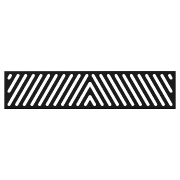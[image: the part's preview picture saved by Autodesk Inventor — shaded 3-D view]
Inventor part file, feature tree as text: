
AUTODESK INVENTOR PART (.ipt)
format: ipt  version: 2015 (Build 190159000, 159)  size: 502,272 bytes
history: native  units: in
note: dims shown in document units (in); Inventor stores cm internally (conversion verified against a paired STEP export)
features: other x5, sheet_metal_op x4, sketch x4, extrude x1, hole x1, fillet x1, imported_body x1
ambient origin geometry x8: Origin, YZ Plane, XZ Plane, XY Plane, X Axis, Y Axis, Z Axis, Center Point
bodies: Body1 (feature_tree)
feature tree (17):
  other  "PartBody"
  other  "Part11"
  extrude  "Extrusion1"  Depth=0.09in
  sheet_metal_op  "Flange1"
  sheet_metal_op  "Flange2"
  hole  "Hole1"  [1 undecoded]
  fillet  "Fillet1"  Radius=0.36in
  imported_body  "Base1"
  sketch  "Sketch1"  dims[d0=0.09in d1=0.045in]
  other  "Plate1"
  sheet_metal_op  "Bend1"
  sketch  "Sketch2"  dims[d2=0.18in d3=0.09in]
  other  "Plate2"
  sheet_metal_op  "Bend2"
  sketch  "Sketch3"  dims[d4=1.18in d5=90.0deg d6=0.09in d7=0.36in]
  sketch  "Sketch4"  dims[d8=0.09in d9=0.09in d10=0.09in d11=0.045in d12=0.18in d13=0.09in d14=1.18in d15=90.0deg d16=0.09in d17=0.36in d18=0.09in d19=0.09in d20=0.5in d21=0.5in d22=11.0236in d24=1.0in d25=0.3937in d27=1.0in d29=0.266in d30=0.75in d31=0.375in d32=0.25in d33=0.5635in d34=0.09in d35=0.8108in d36=0.035in d37=0.035in d38=1.0in d39=0.0in d40=0.125in]
  other  "Definition1"
note: 1 required parameter value undecoded (feature->parameter linkage not recoverable at this tier; creation-order binding heuristic only, values carry confidence <= 0.55)
